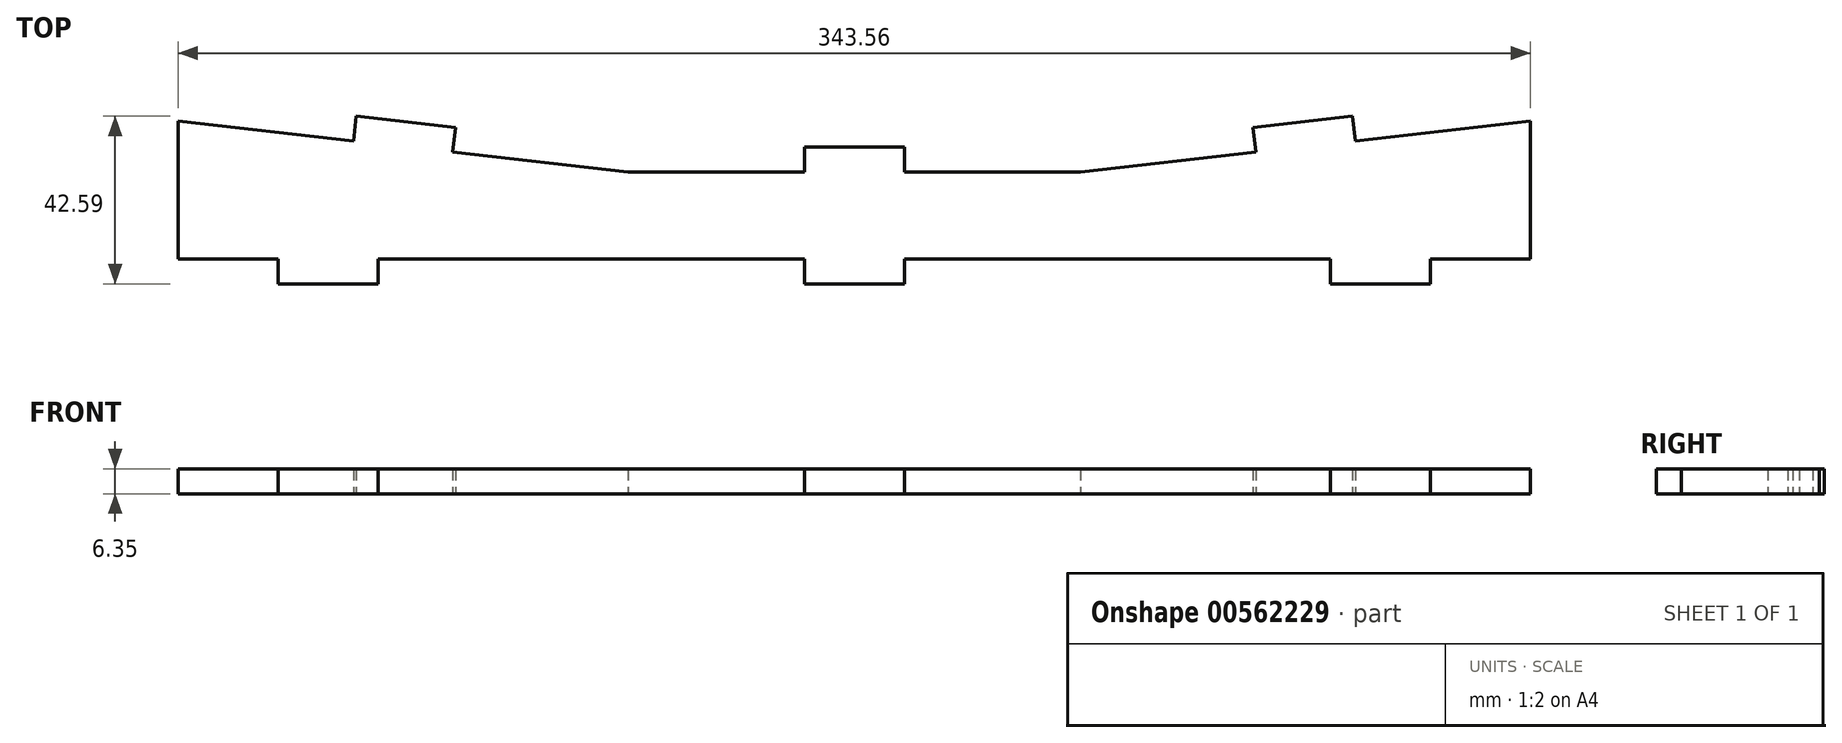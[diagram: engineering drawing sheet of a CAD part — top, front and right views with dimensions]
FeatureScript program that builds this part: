
annotation { "Feature Type Name" : "Feature", "Feature Type Description" : "" }
export const myFeature = defineFeature(function(context is Context, id is Id, definition is map)
    precondition{}
    {
        {
            var Q0;
            Q0=qCreatedBy(makeId("Top.planeOp"),FACE);
            var sketch = newSketch(context, id + "F0", { "sketchPlane" : qUnion([Q0])});
            skLineSegment(sketch, "E0", {"start": v(-171.78, 0) * mm, "end": v(171.78, 0) * mm});
            skLineSegment(sketch, "E1", {"start": v(-171.78, 0) * mm, "end": v(-171.78, 35) * mm});
            skLineSegment(sketch, "E2", {"start": v(-171.78, 35) * mm, "end": v(-57.5, 22) * mm});
            skLineSegment(sketch, "E3", {"start": v(-57.5, 22) * mm, "end": v(57.5, 22) * mm});
            skLineSegment(sketch, "E4", {"start": v(57.5, 22) * mm, "end": v(171.78, 35) * mm});
            skLineSegment(sketch, "E5", {"start": v(171.78, 35) * mm, "end": v(171.78, 0) * mm});
            skPoint(sketch, "E6.orphan", {"position": v(236.34, 0) * mm});
            skLineSegment(sketch, "E7", {"start": v(-146.38, 0) * mm, "end": v(-146.38, -6.35) * mm});
            skLineSegment(sketch, "E8", {"start": v(-146.38, -6.35) * mm, "end": v(-120.98, -6.35) * mm});
            skLineSegment(sketch, "E9", {"start": v(-120.98, -6.35) * mm, "end": v(-120.98, 0) * mm});
            skLineSegment(sketch, "E10", {"start": v(146.38, 0) * mm, "end": v(146.38, -6.35) * mm});
            skLineSegment(sketch, "E11", {"start": v(146.38, -6.35) * mm, "end": v(120.98, -6.35) * mm});
            skLineSegment(sketch, "E12", {"start": v(120.98, -6.35) * mm, "end": v(120.98, 0) * mm});
            skLineSegment(sketch, "E13", {"start": v(-12.7, 0) * mm, "end": v(-12.7, -6.35) * mm});
            skLineSegment(sketch, "E14", {"start": v(-12.7, -6.35) * mm, "end": v(12.7, -6.35) * mm});
            skLineSegment(sketch, "E15", {"start": v(12.7, -6.35) * mm, "end": v(12.7, 0) * mm});
            skLineSegment(sketch, "E16", {"start": v(-127.26, 29.93) * mm, "end": v(-126.54, 36.24) * mm});
            skLineSegment(sketch, "E17", {"start": v(-126.54, 36.24) * mm, "end": v(-101.3, 33.37) * mm});
            skLineSegment(sketch, "E18", {"start": v(-101.3, 33.37) * mm, "end": v(-102.02, 27.06) * mm});
            skLineSegment(sketch, "E19", {"start": v(-12.7, 22) * mm, "end": v(-12.7, 28.35) * mm});
            skLineSegment(sketch, "E20", {"start": v(-12.7, 28.35) * mm, "end": v(12.7, 28.35) * mm});
            skLineSegment(sketch, "E21", {"start": v(12.7, 28.35) * mm, "end": v(12.7, 22) * mm});
            skLineSegment(sketch, "E22", {"start": v(102.02, 27.06) * mm, "end": v(101.3, 33.37) * mm});
            skLineSegment(sketch, "E23", {"start": v(101.3, 33.37) * mm, "end": v(126.54, 36.24) * mm});
            skLineSegment(sketch, "E24", {"start": v(126.54, 36.24) * mm, "end": v(127.26, 29.93) * mm});
            skSolve(sketch);
        }
        {
            var Q0;
            Q0 = qSketchRegion(id + "F0", true);
            extrude(context, id + "F1", {"entities" : qUnion([Q0]), "depth" : 6.35 * mm, "offsetDistance" : 25.4 * mm});
        }
    });
